# Revit family: Domotics-DomesticRanges-GEWISS-SYSTEM_PROTECTION-ONE-WAY_SWITCH_MCB
name_source: partatom
category: Apparecchi elettrici
revit_build: Autodesk Revit 2016 (Build: 20161004_0715(x64)
units: mm (PartAtom-declared; Revit-internal decimal feet)

## family parameters
Condiviso = Sì
Host = Superficie
Mantenere orientamento annotazione = Sì
Punto di calcolo locali = Sì
Quota connettore circolare = Usa diametro
Taglio con vuoti quando caricato = No
Tipo di parte = Normale

## types (15) — shared parameters
Breaking capacity = 3KA
Catalogue = DOMOTICS
Catalogue Range = SYSTEM - DOMESTIC RANGE
Curve = C
Electrocod = 0131
IDF = dfabed87-a10e-49e2-a2e4-dd19fe293aeb
IDT = 4487cd92-e099-4eee-8f2d-522cdc942b38
Immagine tipo = GW21436.jpg
No. SYSTEM modules = 1
Produttore = GEWISS S.p.A.
Prospetto di default = 1219 mm
SEO = MCB
Technical sheet = https://www.gewiss.com
Tipo_ = System Int Magnetotermico_GENERICO : NERO
Type = MCB
URL = https://www.gewiss.com
Version file RFA = 19.4
Voltage = 230V ac
Voltage: = 230V ac

## per-type parameters (varying)
| type | Colour | Description. | Description: | Descrizione | EAN code | Modello | Rated current (A) | Rated current (In) | Type: |
| GW20456 - MCB-1P+N C16 3kA 230V red | Red | One-way switch (1P) | Two-pole (1P+N) | MCB-1P+N C16 3KA 230V SY/RED | 8011564126404 | GW20456 | 16 | 16 | For allocated lines |
| GW20435 - MCB-1P+N C10 3kA 230V white | White | One-way switch (1P+N) | Two-pole (1P+N) | MCB-1P+N C10 3KA 230V SY/WT | 8011564079670 | GW20435 | 10 | 10 |  |
| GW20432 - MCB-1P C10 3kA 230V white | White | One-way switch (1P) | Single pole (1P) | MCB-1P C10 3KA 230V SY/WT | 8011564079649 | GW20432 | 10 | 10 |  |
| GW20431 - MCB-1P C6 3kA 230V white | White | One-way switch (1P) | Single pole (1P) | MCB-1P C6 3KA 230V SY/WT | 8011564079632 | GW20431 | 6 | 6 |  |
| GW20436 - MCB-1P+N C16 3kA 230V white | White | One-way switch (1P+N) | Two-pole (1P+N) | MCB-1P+N C16 3KA 230V SY/WT | 8011564079687 | GW20436 | 16 | 16 |  |
| GW20454 - MCB-1P+N C6 3kA 230V red | Red | One-way switch (1P) | Two-pole (1P+N) | MCB-1P+N C6 3KA 230V SY/RED | 8011564126381 | GW20454 | 6 | 6 | For allocated lines |
| GW20434 - MCB-1P+N C6 3kA 230V white | White | One-way switch (1P+N) | Two-pole (1P+N) | MCB-1P+N C6 3KA 230V SY/WT | 8011564079663 | GW20434 | 6 | 6 |  |
| GW20433 - MCB-1P C16 3kA 230V white | White | One-way switch (1P) | Single pole (1P) | MCB-1P C16 3KA 230V SY/WT | 8011564079656 | GW20433 | 16 | 16 |  |
| GW21436 - MCB-1P+N C16 3kA 230V black | Black | One-way switch (1P+N) | Two-pole (1P+N) | MCB-1P+N C16 3KA 230V SY/BK | 8011564129160 | GW21436 | 16 | 16 |  |
| GW21432 - MCB-1P C10 3kA 230V black | Black | One-way switch (1P) | Single pole (1P) | MCB-1P C10 3KA 230V SY/BK | 8011564129122 | GW21432 | 10 | 10 |  |
| GW20455 - MCB-1P+N C10 3kA 230V red | Red | One-way switch (1P) | Two-pole (1P+N) | MCB-1P+N C10 3KA 230V SY/RED | 8011564126398 | GW20455 | 10 | 10 | For allocated lines |
| GW21431 - MCB-1P C6 3kA 230V black | Black | One-way switch (1P) | Single pole (1P) | MCB-1P C6 3KA 230V SY/BK | 8011564129115 | GW21431 | 6 | 6 |  |
| GW21434 - MCB-1P+N C6 3kA 230V black | Black | One-way switch (1P+N) | Two-pole (1P+N) | MCB-1P+N C6 3KA 230V SY/BK | 8011564129146 | GW21434 | 6 | 6 |  |
| GW21435 - MCB-1P+N C10 3kA 230V black | Black | One-way switch (1P+N) | Two-pole (1P+N) | MCB-1P+N C10 3KA 230V SY/BK | 8011564129153 | GW21435 | 10 | 10 |  |
| GW21433 - MCB-1P C16 3kA 230V black | Black | One-way switch (1P) | Single pole (1P) | MCB-1P C16 3KA 230V SY/BK | 8011564129139 | GW21433 | 16 | 16 |  |

## geometry (parser evidence)
native form markers: Sweep x2
no freeform markers — native parametric forms only
